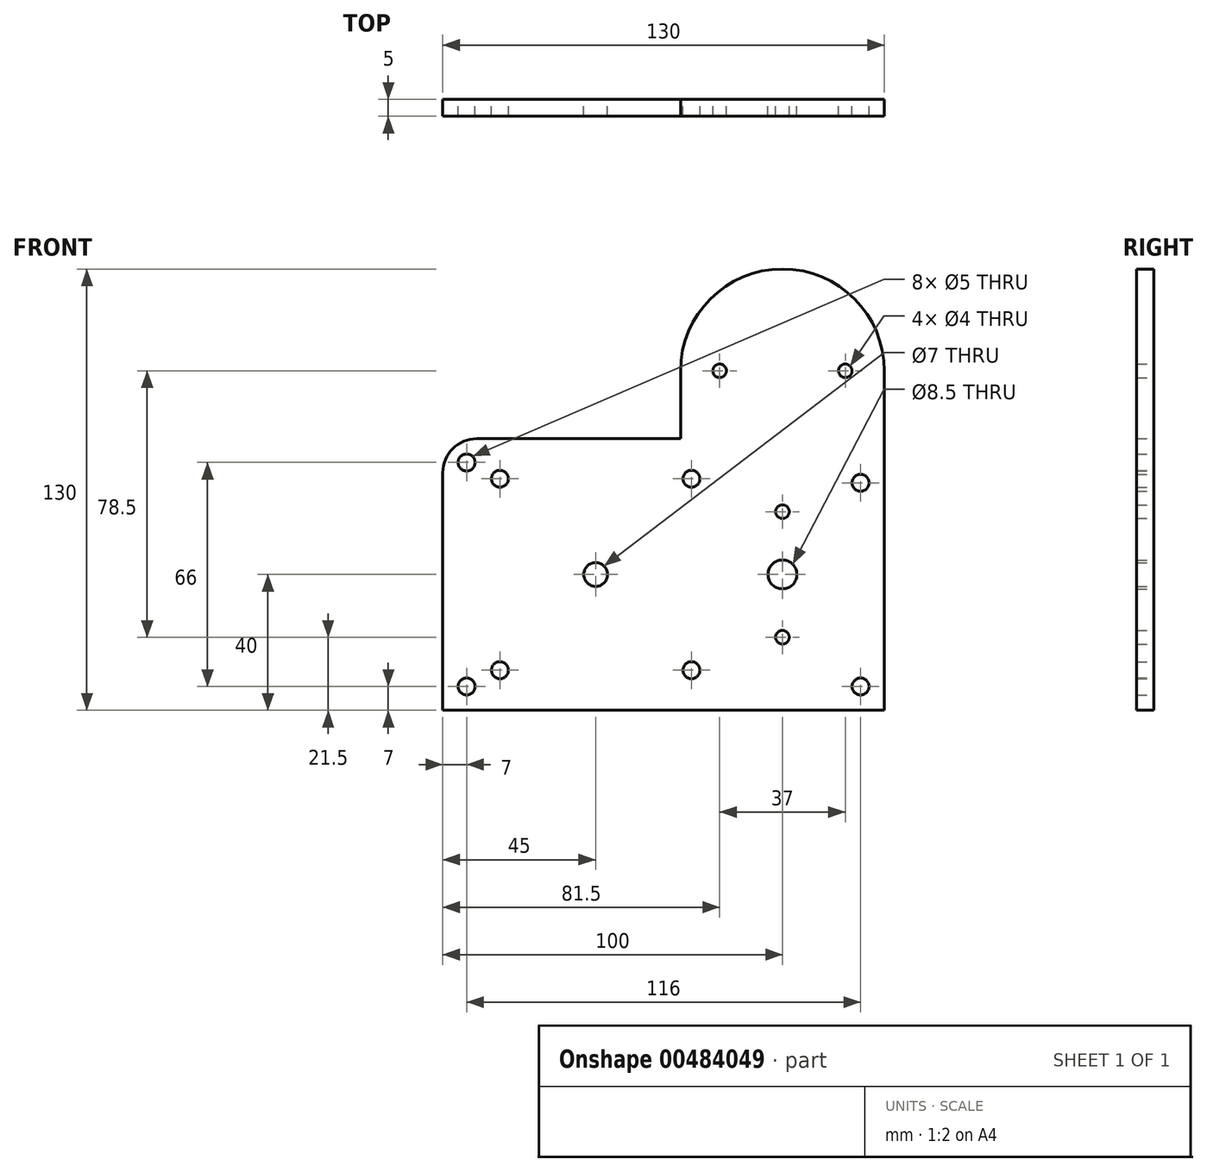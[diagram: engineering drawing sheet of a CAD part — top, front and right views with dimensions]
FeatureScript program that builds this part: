
annotation { "Feature Type Name" : "Feature", "Feature Type Description" : "" }
export const myFeature = defineFeature(function(context is Context, id is Id, definition is map)
    precondition{}
    {
        {
            var Q0;
            Q0=qCreatedBy(makeId("Front.planeOp"),FACE);
            var sketch = newSketch(context, id + "F0", { "sketchPlane" : qUnion([Q0])});
            skCircle(sketch, "E0", {"center": v(-18.5, 10) * mm, "radius": 2 * mm});
            skCircle(sketch, "E1", {"center": v(18.5, 10) * mm, "radius": 2 * mm});
            skLineSegment(sketch, "E2", {"start": v(30, -90) * mm, "end": v(-100, -90) * mm});
            skLineSegment(sketch, "E3", {"start": v(-100, -90) * mm, "end": v(-100, -20) * mm});
            skLineSegment(sketch, "E4", {"start": v(-30, -10) * mm, "end": v(-90, -10) * mm});
            skArc(sketch, "E5", {"start": v(-100, -20) * mm, "mid": v(-97.07, -12.93) * mm, "end": v(-90, -10) * mm});
            skCircle(sketch, "E6", {"center": v(-55, -50) * mm, "radius": 3.5 * mm});
            skCircle(sketch, "E7", {"center": v(-83.2, -21.8) * mm, "radius": 2.5 * mm});
            skCircle(sketch, "E8", {"center": v(-26.8, -21.8) * mm, "radius": 2.5 * mm});
            skCircle(sketch, "E9", {"center": v(-26.8, -78.2) * mm, "radius": 2.5 * mm});
            skCircle(sketch, "E10", {"center": v(-83.2, -78.2) * mm, "radius": 2.5 * mm});
            skLineSegment(sketch, "E11", {"start": v(-30, -10) * mm, "end": v(-30, 10) * mm});
            skLineSegment(sketch, "E12", {"start": v(30, -90) * mm, "end": v(30, 10) * mm});
            skArc(sketch, "E13", {"start": v(-30, 10) * mm, "mid": v(0, 40) * mm, "end": v(30, 10) * mm});
            skCircle(sketch, "E14", {"center": v(0, -31.5) * mm, "radius": 2 * mm});
            skCircle(sketch, "E15", {"center": v(0, -68.5) * mm, "radius": 2 * mm});
            skCircle(sketch, "E16", {"center": v(23, -23) * mm, "radius": 2.5 * mm});
            skCircle(sketch, "E17", {"center": v(23, -83) * mm, "radius": 2.5 * mm});
            skCircle(sketch, "E18", {"center": v(-93, -83) * mm, "radius": 2.5 * mm});
            skCircle(sketch, "E19", {"center": v(-93, -17) * mm, "radius": 2.5 * mm});
            skLineSegment(sketch, "E20", {"start": v(0, -31.5) * mm, "end": v(0, -50) * mm});
            skLineSegment(sketch, "E21", {"start": v(0, -50) * mm, "end": v(0, -68.5) * mm});
            skCircle(sketch, "E22", {"center": v(0, -50) * mm, "radius": 4.25 * mm});
            skSolve(sketch);
        }
        {
            var Q0;
            Q0=makeQuery(id+"F0.imprint","IMPRINT",FACE,{"disambiguationData":[TD([[makeQuery(id+"F0.imprint","IMPRINT",EDGE,{"derivedFrom":sQuery(id+"F0.wireOp",EDGE,"E0")}),-1.0]])]});
            extrude(context, id + "F1", {"entities" : qUnion([Q0]), "depth" : 5 * mm});
        }
    });
